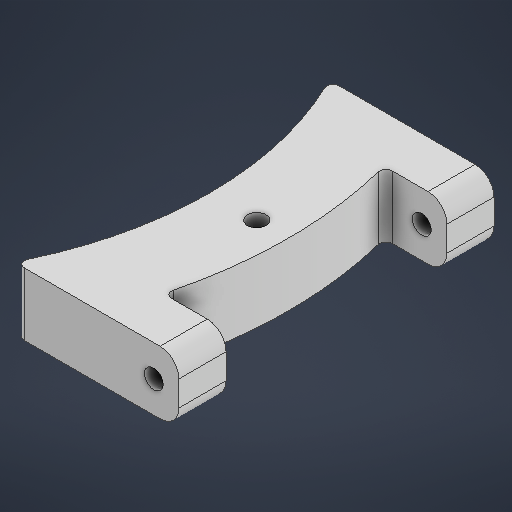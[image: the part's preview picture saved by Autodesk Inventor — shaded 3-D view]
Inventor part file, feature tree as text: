
AUTODESK INVENTOR PART (.ipt)
format: ipt  version: 2025 (Build 290162000, 162)  size: 301,056 bytes
history: native  units: in
note: dims shown in document units (in); Inventor stores cm internally (conversion verified against a paired STEP export)
features: sketch x6, fillet x4, extrude x3, hole x2, mirror x2, projected_geometry x1
ambient origin geometry x8: Origin, YZ Plane, XZ Plane, XY Plane, X Axis, Y Axis, Z Axis, Center Point
bodies: Solid1 (feature_tree)
feature tree (18):
  extrude  "Extrusion1"  Depth=8.6614in
  extrude  "Extrusion3"  Depth=3.9469in
  fillet  "Fillet1"  Radius=0.9843in
  fillet  "Fillet2"  Radius=0.5906in
  fillet  "Fillet3"  Radius=0.7874in
  hole  "Hole2"  [1 undecoded]
  mirror  "Mirror1"
  mirror  "Mirror2"
  hole  "Hole3"  [1 undecoded]
  extrude  "Extrusion7"  Depth=0.2362in
  fillet  "Fillet7"  Radius=0.3937in
  sketch  "Sketch1"  dims[d0=10.6299in d1=8.6614in]
  sketch  "Sketch4"  dims[d25=0.5906in d26=0.0in d27=0.0in]
  projected_geometry  "Projected Loop1"
  sketch  "Sketch5"  dims[d28=0.2362in d29=0.3937in]
  sketch  "Sketch7"  dims[d30=0.0787in]
  sketch  "Sketch10"  dims[d31=0.2362in d32=0.2362in d33=0.3465in d34=0.1969in d35=90.0deg d36=0.315in d37=0.8108in d38=0.315in d39=0.3937in d43=0.1969in d44=0.2362in d45=0.1575in d46=0.0787in d47=90.0deg d48=0.315in d49=0.8108in d50=5.0197in d57=0.3937in d61=0.0in d62=0.0in d63=0.0787in d68=9.8425in d74=0.2362in d75=3.937in d77=360.0deg]
  sketch  "Sketch Circular Pattern3"  dims[d2=0.7874in d3=0.0in d21=3.9469in d22=0.9843in d23=0.5906in d24=0.7874in]
note: 2 required parameter values undecoded (feature->parameter linkage not recoverable at this tier; creation-order binding heuristic only, values carry confidence <= 0.55)
